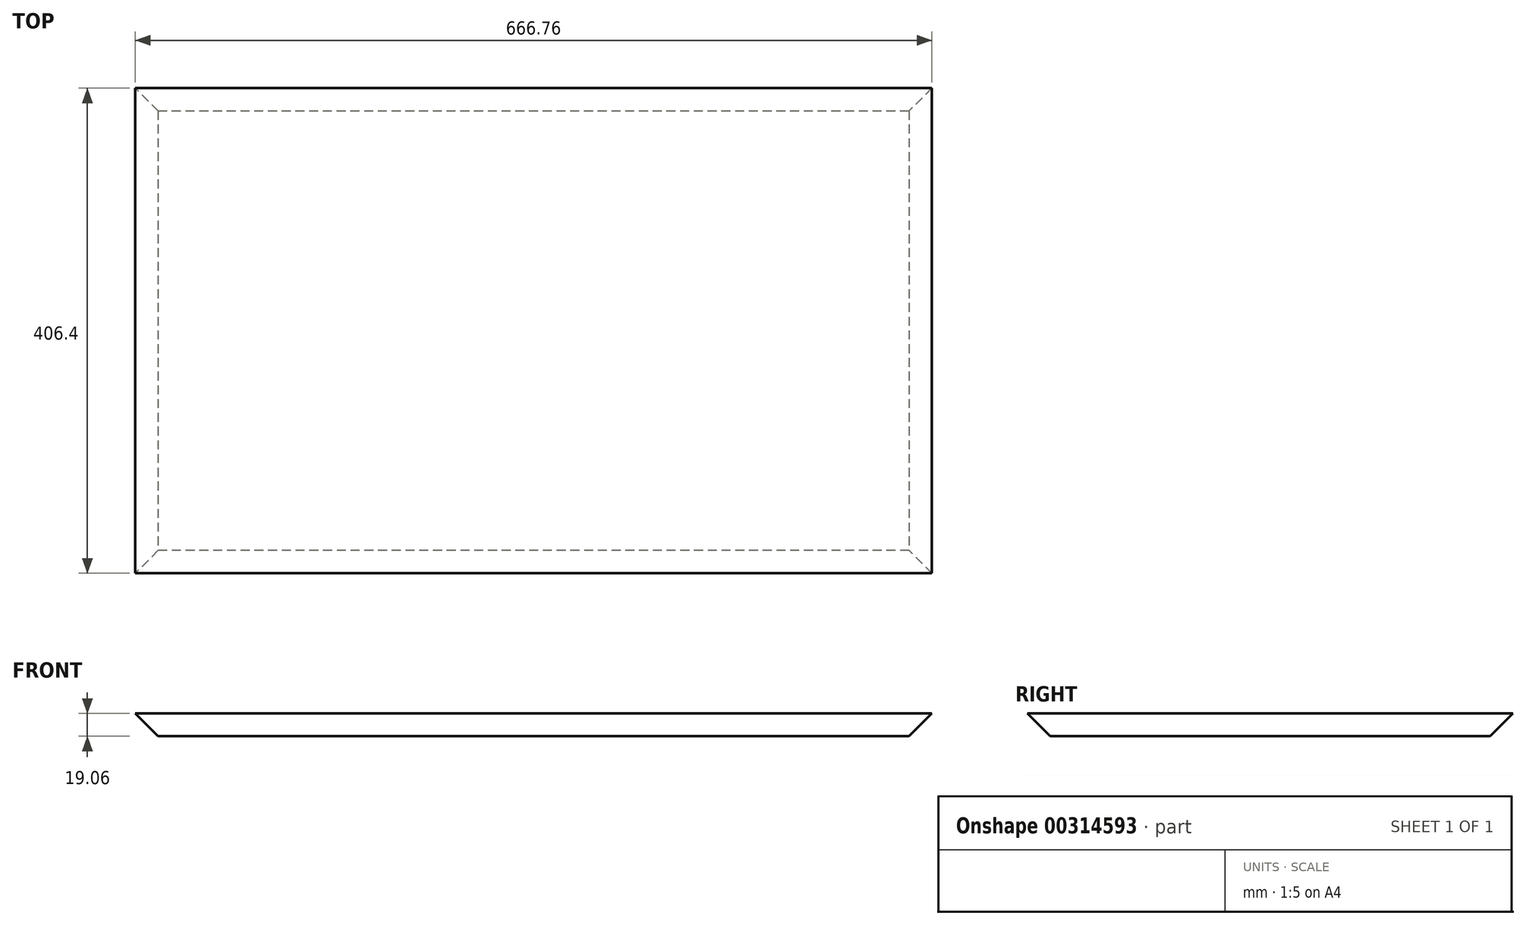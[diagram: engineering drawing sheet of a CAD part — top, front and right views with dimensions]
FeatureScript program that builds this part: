
annotation { "Feature Type Name" : "Feature", "Feature Type Description" : "" }
export const myFeature = defineFeature(function(context is Context, id is Id, definition is map)
    precondition{}
    {
        {
            var Q0;
            Q0=qCreatedBy(makeId("Front.planeOp"),FACE);
            var sketch = newSketch(context, id + "F0", { "sketchPlane" : qUnion([Q0])});
            skLineSegment(sketch, "E0", {"start": v(-333.38, 9.52) * mm, "end": v(333.38, 9.52) * mm});
            skLineSegment(sketch, "E1", {"start": v(333.38, 9.53) * mm, "end": v(314.33, -9.52) * mm});
            skLineSegment(sketch, "E2", {"start": v(314.33, -9.53) * mm, "end": v(-314.33, -9.53) * mm});
            skLineSegment(sketch, "E3", {"start": v(-314.33, -9.53) * mm, "end": v(-333.38, 9.53) * mm});
            skLineSegment(sketch, "E4", {"start": v(0, 9.53) * mm, "end": v(0, -9.53) * mm, "construction": true});
            skSolve(sketch);
        }
        {
            var Q0;
            Q0=qSketchRegion(id+"F0",true);
            extrude(context, id + "F1", {"entities" : qUnion([Q0]), "oppositeDirection" : true, "depth" : 406.4 * mm});
        }
        {
            var Q0;
            Q0=makeQuery(id+"F1.opExtrude","CAP_EDGE",EDGE,{"disambiguationData":[OSD([sQuery(id+"F0.wireOp",EDGE,"E2")])],"isStart":false});
            chamfer(context, id + "F2", {"entities" : qUnion([Q0]), "width" : 19.05 * mm, "tangentPropagation" : true});
        }
        {
            var Q0;
            Q0=makeQuery(id+"F1.opExtrude","CAP_EDGE",EDGE,{"disambiguationData":[OSD([sQuery(id+"F0.wireOp",EDGE,"E2")])],"isStart":true});
            chamfer(context, id + "F3", {"entities" : qUnion([Q0]), "width" : 19.05 * mm, "tangentPropagation" : true});
        }
    });
